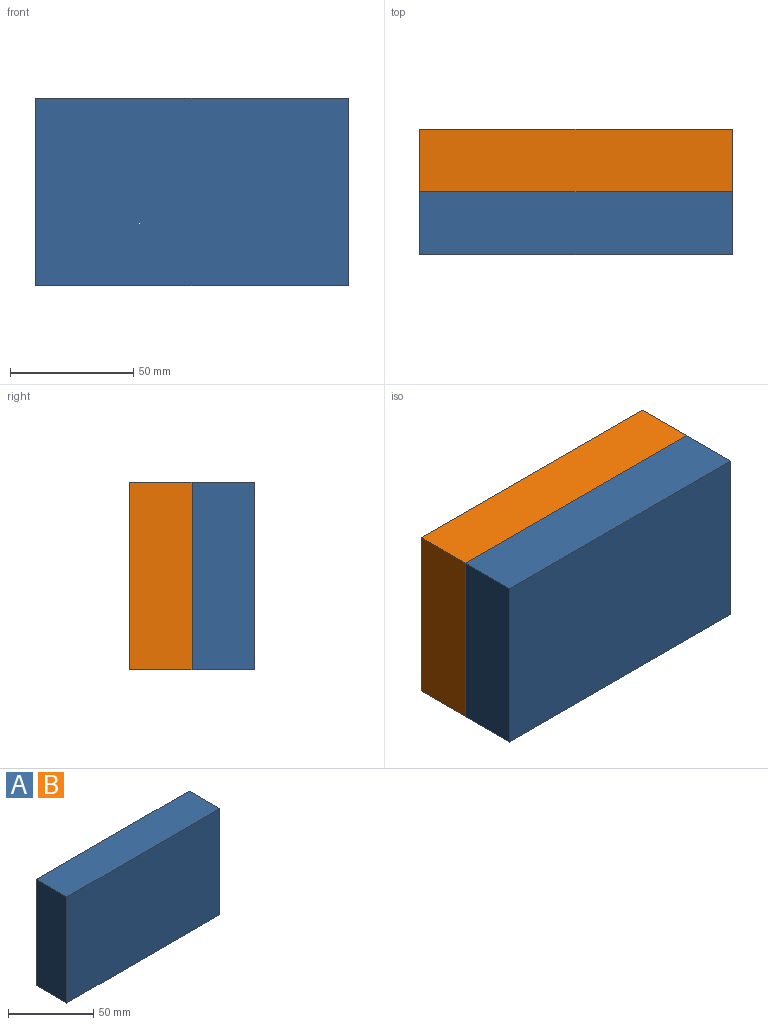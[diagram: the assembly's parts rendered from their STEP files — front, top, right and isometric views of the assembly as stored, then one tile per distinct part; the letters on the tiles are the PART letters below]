
ASSEMBLY  parts=2 mates=1
PART A: 6 faces, bbox 127x25.4x76.2 mm
  f0: plane 76.2x25.4mm, normal (-1,0,0), area 1935.5mm2, adj f1,f3,f4,f5
  f1: plane 127x25.4mm, normal (0,0,-1), area 3225.8mm2, adj f0,f2,f4,f5
  f2: plane 76.2x25.4mm, normal (1,0,0), area 1935.5mm2, adj f1,f3,f4,f5
  f3: plane 127x25.4mm, normal (0,0,1), area 3225.8mm2, adj f0,f2,f4,f5
  f4: plane 127x76.2mm, normal (0,-1,0), area 9677.4mm2, adj f0,f1,f2,f3
  f5: plane 127x76.2mm, normal (0,1,0), area 9677.4mm2, adj f0,f1,f2,f3
PART B: same geometry as A
PLACE A t=(-41.26,0,-71.55)mm
PLACE B t=(-41.26,25.4,-71.55)mm
MATE fastened B.f4 <-> A.f5  axis (0,-1,0) through (-22.81,0,-66.17)mm
